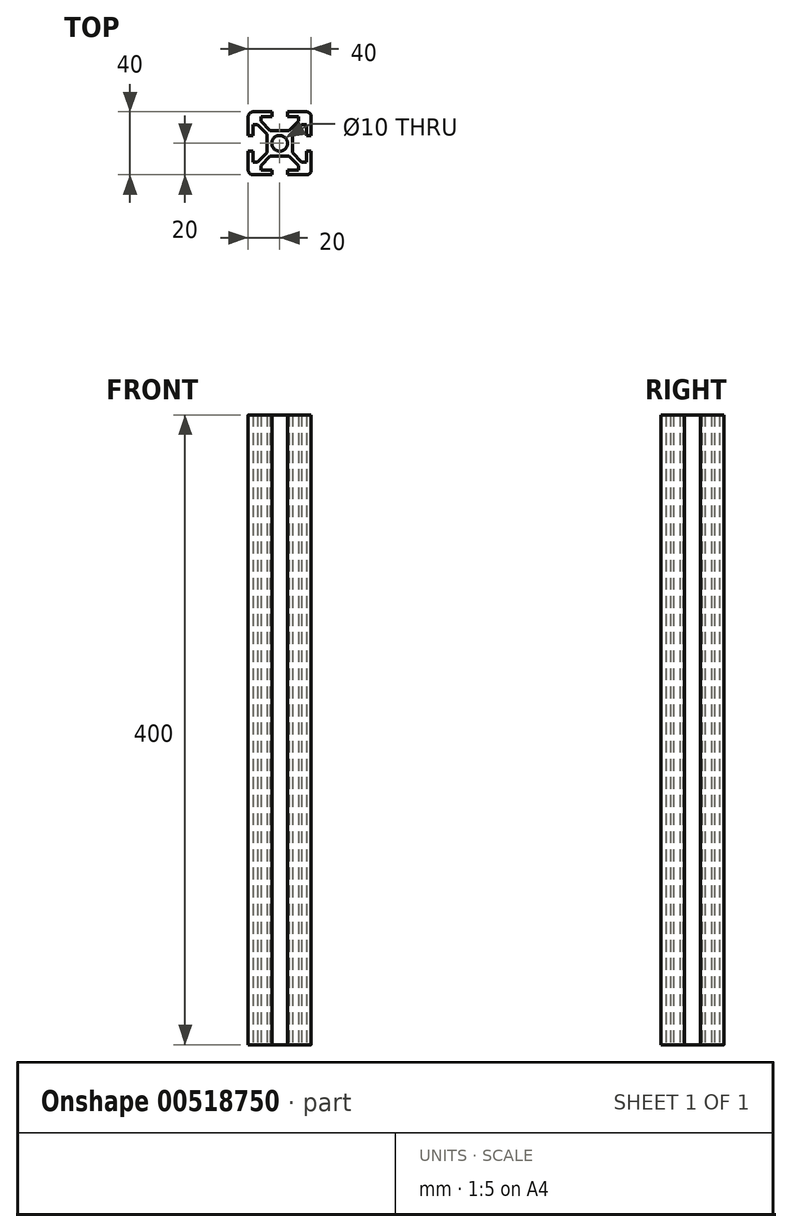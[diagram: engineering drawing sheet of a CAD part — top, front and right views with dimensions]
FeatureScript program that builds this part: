
annotation { "Feature Type Name" : "Feature", "Feature Type Description" : "" }
export const myFeature = defineFeature(function(context is Context, id is Id, definition is map)
    precondition{}
    {
        {
            var Q0;
            Q0=qCreatedBy(makeId("Top.planeOp"),FACE);
            var sketch = newSketch(context, id + "F0", { "sketchPlane" : qUnion([Q0])});
            skLineSegment(sketch, "E0.bottom", {"start": v(17, 20) * mm, "end": v(-17, 20) * mm});
            skLineSegment(sketch, "E0.top", {"start": v(17, -20) * mm, "end": v(-17, -20) * mm});
            skLineSegment(sketch, "E0.left", {"start": v(20, 17) * mm, "end": v(20, -17) * mm});
            skLineSegment(sketch, "E0.right", {"start": v(-20, 17) * mm, "end": v(-20, -17) * mm});
            skPoint(sketch, "E0.middle", {"position": v(0, 0) * mm});
            skPoint(sketch, "E1.visualSharp", {"position": v(-20, 20) * mm});
            skArc(sketch, "E1.filletArc", {"start": v(-17, 20) * mm, "mid": v(-19.12, 19.12) * mm, "end": v(-20, 17) * mm});
            skPoint(sketch, "E2.visualSharp", {"position": v(20, 20) * mm});
            skArc(sketch, "E2.filletArc", {"start": v(20, 17) * mm, "mid": v(19.12, 19.12) * mm, "end": v(17, 20) * mm});
            skPoint(sketch, "E3.visualSharp", {"position": v(20, -20) * mm});
            skArc(sketch, "E3.filletArc", {"start": v(17, -20) * mm, "mid": v(19.12, -19.12) * mm, "end": v(20, -17) * mm});
            skPoint(sketch, "E4.visualSharp", {"position": v(-20, -20) * mm});
            skArc(sketch, "E4.filletArc", {"start": v(-20, -17) * mm, "mid": v(-19.12, -19.12) * mm, "end": v(-17, -20) * mm});
            skCircle(sketch, "E5", {"center": v(0, 0) * mm, "radius": 5 * mm});
            skLineSegment(sketch, "E6", {"start": v(0, 8) * mm, "end": v(6, 8) * mm});
            skLineSegment(sketch, "E7", {"start": v(6, 8) * mm, "end": v(12, 14) * mm});
            skLineSegment(sketch, "E8", {"start": v(12, 14) * mm, "end": v(12, 17) * mm});
            skLineSegment(sketch, "E9", {"start": v(12, 17) * mm, "end": v(5, 17) * mm});
            skLineSegment(sketch, "E10", {"start": v(5, 17) * mm, "end": v(5, 20) * mm});
            skLineSegment(sketch, "E11.MirrorCS", {"start": v(0, 8) * mm, "end": v(-6, 8) * mm});
            skLineSegment(sketch, "E12.MirrorCS", {"start": v(-12, 14) * mm, "end": v(-12, 17) * mm});
            skLineSegment(sketch, "E13.MirrorCS", {"start": v(-6, 8) * mm, "end": v(-12, 14) * mm});
            skLineSegment(sketch, "E14.MirrorCS", {"start": v(-5, 17) * mm, "end": v(-5, 20) * mm});
            skLineSegment(sketch, "E15.MirrorCS", {"start": v(-12, 17) * mm, "end": v(-5, 17) * mm});
            skLineSegment(sketch, "E16.1.0", {"start": v(-8, 0) * mm, "end": v(-8, -6) * mm});
            skLineSegment(sketch, "E16.1.1", {"start": v(-8, 0) * mm, "end": v(-8, 6) * mm});
            skLineSegment(sketch, "E16.1.2", {"start": v(-8, 6) * mm, "end": v(-14, 12) * mm});
            skLineSegment(sketch, "E16.1.3", {"start": v(-17, 12) * mm, "end": v(-17, 5) * mm});
            skLineSegment(sketch, "E16.1.4", {"start": v(-17, -12) * mm, "end": v(-17, -5) * mm});
            skLineSegment(sketch, "E16.1.5", {"start": v(-8, -6) * mm, "end": v(-14, -12) * mm});
            skLineSegment(sketch, "E16.1.6", {"start": v(-14, -12) * mm, "end": v(-17, -12) * mm});
            skLineSegment(sketch, "E16.1.7", {"start": v(-14, 12) * mm, "end": v(-17, 12) * mm});
            skLineSegment(sketch, "E16.1.8", {"start": v(-17, 5) * mm, "end": v(-20, 5) * mm});
            skLineSegment(sketch, "E16.1.9", {"start": v(-17, -5) * mm, "end": v(-20, -5) * mm});
            skLineSegment(sketch, "E16.2.0", {"start": v(0, -8) * mm, "end": v(6, -8) * mm});
            skLineSegment(sketch, "E16.2.1", {"start": v(0, -8) * mm, "end": v(-6, -8) * mm});
            skLineSegment(sketch, "E16.2.2", {"start": v(-6, -8) * mm, "end": v(-12, -14) * mm});
            skLineSegment(sketch, "E16.2.3", {"start": v(-12, -17) * mm, "end": v(-5, -17) * mm});
            skLineSegment(sketch, "E16.2.4", {"start": v(12, -17) * mm, "end": v(5, -17) * mm});
            skLineSegment(sketch, "E16.2.5", {"start": v(6, -8) * mm, "end": v(12, -14) * mm});
            skLineSegment(sketch, "E16.2.6", {"start": v(12, -14) * mm, "end": v(12, -17) * mm});
            skLineSegment(sketch, "E16.2.7", {"start": v(-12, -14) * mm, "end": v(-12, -17) * mm});
            skLineSegment(sketch, "E16.2.8", {"start": v(-5, -17) * mm, "end": v(-5, -20) * mm});
            skLineSegment(sketch, "E16.2.9", {"start": v(5, -17) * mm, "end": v(5, -20) * mm});
            skLineSegment(sketch, "E16.3.0", {"start": v(8, 0) * mm, "end": v(8, 6) * mm});
            skLineSegment(sketch, "E16.3.1", {"start": v(8, 0) * mm, "end": v(8, -6) * mm});
            skLineSegment(sketch, "E16.3.2", {"start": v(8, -6) * mm, "end": v(14, -12) * mm});
            skLineSegment(sketch, "E16.3.3", {"start": v(17, -12) * mm, "end": v(17, -5) * mm});
            skLineSegment(sketch, "E16.3.4", {"start": v(17, 12) * mm, "end": v(17, 5) * mm});
            skLineSegment(sketch, "E16.3.5", {"start": v(8, 6) * mm, "end": v(14, 12) * mm});
            skLineSegment(sketch, "E16.3.6", {"start": v(14, 12) * mm, "end": v(17, 12) * mm});
            skLineSegment(sketch, "E16.3.7", {"start": v(14, -12) * mm, "end": v(17, -12) * mm});
            skLineSegment(sketch, "E16.3.8", {"start": v(17, -5) * mm, "end": v(20, -5) * mm});
            skLineSegment(sketch, "E16.3.9", {"start": v(17, 5) * mm, "end": v(20, 5) * mm});
            skSolve(sketch);
        }
        {
            var Q0;
            {var subQ4=sQuery(id+"F0.wireOp",EDGE,"E1.filletArc");Q0=makeQuery(id+"F0.imprint","IMPRINT",FACE,{"disambiguationData":[TD([[makeQuery(id+"F0.imprint","IMPRINT",EDGE,{"derivedFrom":subQ4}),1.0]])]});}
            extrude(context, id + "F1", {"entities" : qUnion([Q0]), "depth" : 400 * mm, "offsetDistance" : 25 * mm});
        }
    });
